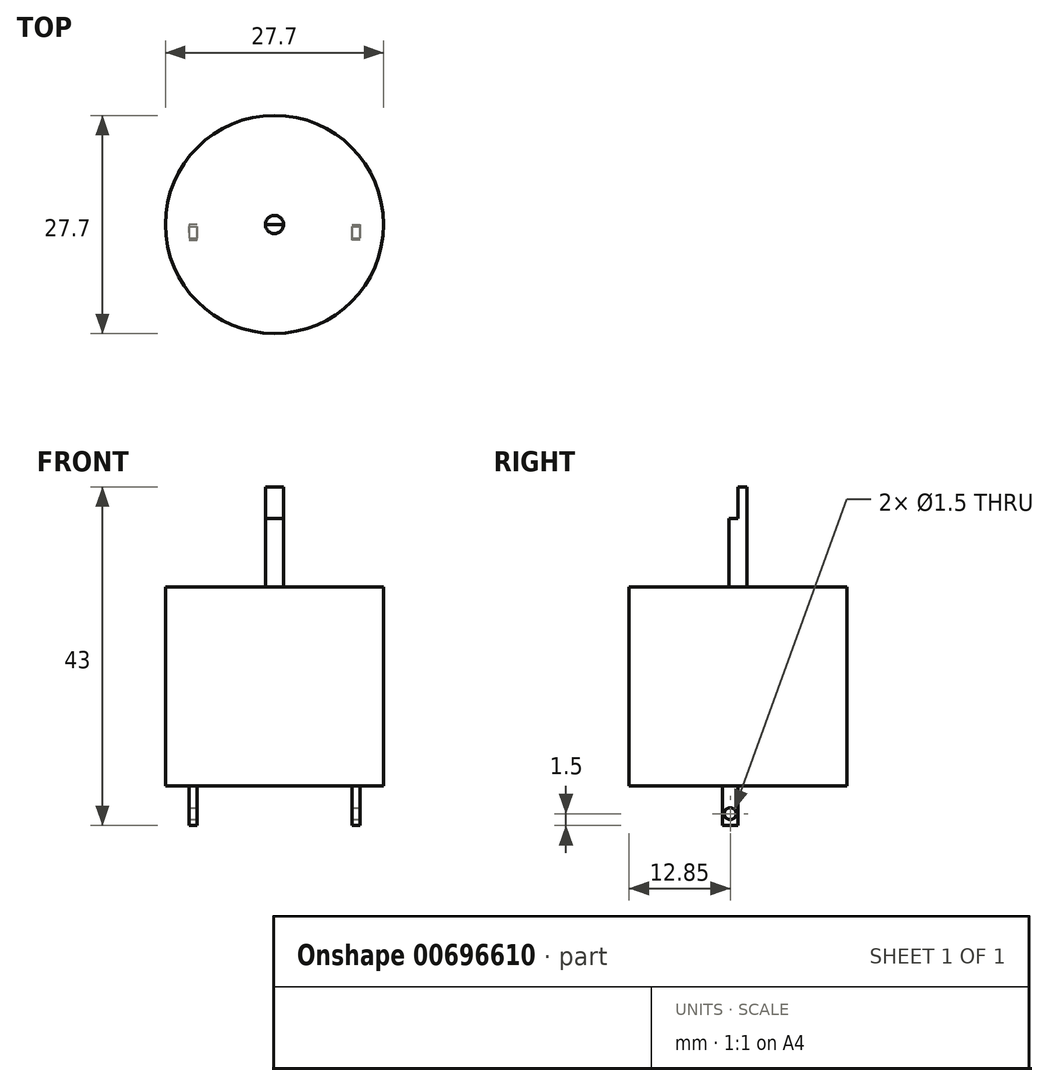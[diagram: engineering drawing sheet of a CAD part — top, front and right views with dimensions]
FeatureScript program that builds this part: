
annotation { "Feature Type Name" : "Feature", "Feature Type Description" : "" }
export const myFeature = defineFeature(function(context is Context, id is Id, definition is map)
    precondition{}
    {
        {
            var Q0;
            Q0=qCreatedBy(makeId("Top.planeOp"),FACE);
            var sketch = newSketch(context, id + "F0", { "sketchPlane" : qUnion([Q0])});
            skCircle(sketch, "E0", {"center": v(0, 0) * mm, "radius": 13.85 * mm});
            skSolve(sketch);
        }
        {
            var Q0;
            Q0 = qSketchRegion(id + "F0", true);
            extrude(context, id + "F1", {"entities" : qUnion([Q0]), "depth" : 25.3 * mm, "offsetDistance" : 25 * mm});
        }
        {
            var Q0;
            Q0=makeQuery(id+"F1.opExtrude","CAP_FACE",FACE,{"disambiguationData":[OSD([sQuery(id+"F0.wireOp",EDGE,"E0")])],"isStart":false});
            var sketch = newSketch(context, id + "F2", { "sketchPlane" : qUnion([Q0])});
            skCircle(sketch, "E1", {"center": v(0, 0) * mm, "radius": 1.15 * mm});
            skSolve(sketch);
        }
        {
            var Q0;
            Q0 = qSketchRegion(id + "F2", true);
            extrude(context, id + "F3", {"entities" : qUnion([Q0]), "operationType" : NewBodyOperationType.ADD, "depth" : 12.7 * mm, "offsetDistance" : 25 * mm});
        }
        {
            var Q0;
            Q0=qCreatedBy(makeId("Right.planeOp"),FACE);
            cPlane(context, id + "F4", {"entities" : qUnion([Q0]), "cplaneType" : CPlaneType.OFFSET, "offset" : 1.15 * mm, "width" : 150 * mm, "height" : 150 * mm});
        }
        {
            var Q0;
            Q0=qCreatedBy(id+"F4.planeOp",FACE);
            var sketch = newSketch(context, id + "F5", { "sketchPlane" : qUnion([Q0])});
            skLineSegment(sketch, "E2", {"start": v(-1.16, 38.01) * mm, "end": v(0, 38.01) * mm});
            skLineSegment(sketch, "E3", {"start": v(0, 38.01) * mm, "end": v(0, 34.02) * mm});
            skLineSegment(sketch, "E4", {"start": v(0, 34.02) * mm, "end": v(-1.22, 34.02) * mm});
            skLineSegment(sketch, "E5", {"start": v(-1.22, 34.02) * mm, "end": v(-1.16, 38.01) * mm});
            skSolve(sketch);
        }
        {
            var Q0;
            Q0 = qSketchRegion(id + "F5", true);
            extrude(context, id + "F6", {"entities" : qUnion([Q0]), "operationType" : NewBodyOperationType.REMOVE, "oppositeDirection" : true, "depth" : 25 * mm, "offsetDistance" : 25 * mm});
        }
        {
            var Q0;
            Q0=makeQuery(id+"F1.opExtrude","CAP_FACE",FACE,{"disambiguationData":[OSD([sQuery(id+"F0.wireOp",EDGE,"E0")])],"isStart":true});
            var sketch = newSketch(context, id + "F7", { "sketchPlane" : qUnion([Q0])});
            skLineSegment(sketch, "E6", {"start": v(-10.85, 0) * mm, "end": v(-10.85, 2) * mm});
            skLineSegment(sketch, "E7", {"start": v(-10.85, 2) * mm, "end": v(-9.85, 2) * mm});
            skLineSegment(sketch, "E8", {"start": v(-9.85, 2) * mm, "end": v(-9.85, 0) * mm});
            skLineSegment(sketch, "E9", {"start": v(-9.85, 0) * mm, "end": v(-10.85, 0) * mm});
            skLineSegment(sketch, "E10.MirrorCS", {"start": v(10.85, 2) * mm, "end": v(9.85, 2) * mm});
            skLineSegment(sketch, "E11.MirrorCS", {"start": v(10.85, 0) * mm, "end": v(10.85, 2) * mm});
            skLineSegment(sketch, "E12.MirrorCS", {"start": v(9.85, 2) * mm, "end": v(9.85, 0) * mm});
            skLineSegment(sketch, "E13.MirrorCS", {"start": v(9.85, 0) * mm, "end": v(10.85, 0) * mm});
            skSolve(sketch);
        }
        {
            var Q0;
            Q0=makeQuery(id+"F7.imprint","IMPRINT",FACE,{"disambiguationData":[TD([[makeQuery(id+"F7.imprint","IMPRINT",EDGE,{"derivedFrom":sQuery(id+"F7.wireOp",EDGE,"E6")}),-1.0]])]});
            var Q1;
            Q1=makeQuery(id+"F7.imprint","IMPRINT",FACE,{"disambiguationData":[TD([[makeQuery(id+"F7.imprint","IMPRINT",EDGE,{"derivedFrom":sQuery(id+"F7.wireOp",EDGE,"E10.MirrorCS")}),1.0]])]});
            extrude(context, id + "F8", {"entities" : qUnion([Q0, Q1]), "operationType" : NewBodyOperationType.ADD, "depth" : 5 * mm, "offsetDistance" : 25 * mm});
        }
        {
            var Q0;
            Q0=makeQuery(id+"F8.opExtrude","SWEPT_FACE",FACE,{"disambiguationData":[OSD([sQuery(id+"F7.wireOp",EDGE,"E11.MirrorCS")])]});
            var sketch = newSketch(context, id + "F9", { "sketchPlane" : qUnion([Q0])});
            skCircle(sketch, "E14", {"center": v(-1, -3.5) * mm, "radius": 0.75 * mm});
            skSolve(sketch);
        }
        {
            var Q0;
            Q0 = qSketchRegion(id + "F9", true);
            extrude(context, id + "F10", {"entities" : qUnion([Q0]), "operationType" : NewBodyOperationType.REMOVE, "endBound" : BoundingType.THROUGH_ALL, "oppositeDirection" : true, "depth" : 25 * mm, "offsetDistance" : 25 * mm});
        }
    });
